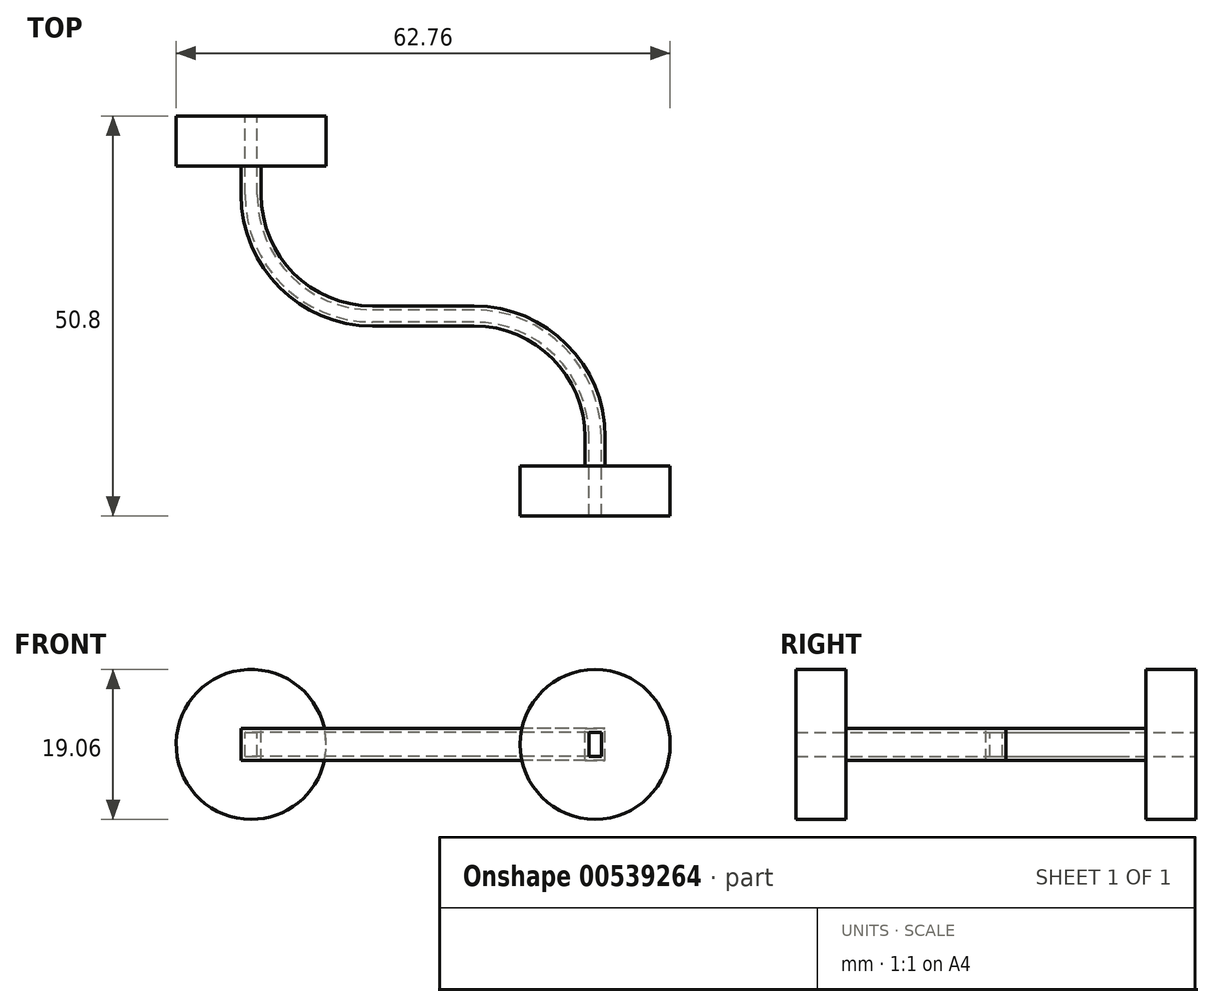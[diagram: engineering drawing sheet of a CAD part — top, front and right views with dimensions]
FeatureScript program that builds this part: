
annotation { "Feature Type Name" : "Feature", "Feature Type Description" : "" }
export const myFeature = defineFeature(function(context is Context, id is Id, definition is map)
    precondition{}
    {
        {
            var Q0;
            Q0=qCreatedBy(makeId("Top.planeOp"),FACE);
            var sketch = newSketch(context, id + "F0", { "sketchPlane" : qUnion([Q0])});
            skLineSegment(sketch, "E0", {"start": v(0, 0) * mm, "end": v(0, 10) * mm});
            skLineSegment(sketch, "E1", {"start": v(0, 0) * mm, "end": v(-21.85, 0) * mm});
            skLineSegment(sketch, "E2", {"start": v(-21.85, 0) * mm, "end": v(-21.85, 25.4) * mm});
            skLineSegment(sketch, "E3", {"start": v(-21.85, 25.4) * mm, "end": v(-15.4, 25.4) * mm});
            skLineSegment(sketch, "E4", {"start": v(-21.85, 25.4) * mm, "end": v(-28.3, 25.4) * mm});
            skLineSegment(sketch, "E5", {"start": v(-21.85, 25.4) * mm, "end": v(-21.85, 50.8) * mm});
            skLineSegment(sketch, "E6", {"start": v(-21.85, 50.8) * mm, "end": v(-43.7, 50.8) * mm});
            skLineSegment(sketch, "E7", {"start": v(-43.7, 50.8) * mm, "end": v(-43.7, 40.8) * mm});
            skArc(sketch, "E8", {"start": v(0, 10) * mm, "mid": v(-4.51, 20.89) * mm, "end": v(-15.4, 25.4) * mm});
            skArc(sketch, "E9", {"start": v(-43.7, 40.8) * mm, "mid": v(-39.19, 29.91) * mm, "end": v(-28.3, 25.4) * mm});
            skSolve(sketch);
        }
        {
            var Q0;
            Q0=qCreatedBy(makeId("Front.planeOp"),FACE);
            var sketch = newSketch(context, id + "F1", { "sketchPlane" : qUnion([Q0])});
            skLineSegment(sketch, "E10.bottom", {"start": v(-0.77, -1.55) * mm, "end": v(0.78, -1.55) * mm});
            skLineSegment(sketch, "E10.top", {"start": v(-0.78, 1.55) * mm, "end": v(0.77, 1.55) * mm});
            skLineSegment(sketch, "E10.left", {"start": v(-0.77, -1.55) * mm, "end": v(-0.78, 1.55) * mm});
            skLineSegment(sketch, "E10.right", {"start": v(0.78, -1.55) * mm, "end": v(0.77, 1.55) * mm});
            skPoint(sketch, "E10.middle", {"position": v(0, 0) * mm});
            skLineSegment(sketch, "E11.bottom", {"start": v(-1.27, -2.05) * mm, "end": v(1.28, -2.05) * mm});
            skLineSegment(sketch, "E11.top", {"start": v(-1.28, 2.05) * mm, "end": v(1.27, 2.05) * mm});
            skLineSegment(sketch, "E11.left", {"start": v(-1.27, -2.05) * mm, "end": v(-1.28, 2.05) * mm});
            skLineSegment(sketch, "E11.right", {"start": v(1.28, -2.05) * mm, "end": v(1.27, 2.05) * mm});
            skCircle(sketch, "E12", {"center": v(0, 0) * mm, "radius": 9.53 * mm});
            skSolve(sketch);
        }
        {
            var Q0;
            Q0=qCreatedBy(makeId("Front.planeOp"),FACE);
            cPlane(context, id + "F2", {"entities" : qUnion([Q0]), "cplaneType" : CPlaneType.OFFSET, "offset" : (25.4 * 2) * mm, "oppositeDirection" : true, "width" : 150 * mm, "height" : 150 * mm});
        }
        {
            var Q0;
            Q0=qCreatedBy(id+"F2.planeOp",FACE);
            var sketch = newSketch(context, id + "F3", { "sketchPlane" : qUnion([Q0])});
            skLineSegment(sketch, "E13.bottom", {"start": v(-42.93, -1.55) * mm, "end": v(-44.48, -1.55) * mm});
            skLineSegment(sketch, "E13.top", {"start": v(-42.93, 1.55) * mm, "end": v(-44.48, 1.55) * mm});
            skLineSegment(sketch, "E13.left", {"start": v(-42.93, -1.55) * mm, "end": v(-42.93, 1.55) * mm});
            skLineSegment(sketch, "E13.right", {"start": v(-44.48, -1.55) * mm, "end": v(-44.48, 1.55) * mm});
            skPoint(sketch, "E13.middle", {"position": v(-43.7, 0) * mm});
            skLineSegment(sketch, "E14.bottom", {"start": v(-42.43, -2.05) * mm, "end": v(-44.98, -2.05) * mm});
            skLineSegment(sketch, "E14.top", {"start": v(-42.43, 2.05) * mm, "end": v(-44.98, 2.05) * mm});
            skLineSegment(sketch, "E14.left", {"start": v(-42.43, -2.05) * mm, "end": v(-42.43, 2.05) * mm});
            skLineSegment(sketch, "E14.right", {"start": v(-44.98, -2.05) * mm, "end": v(-44.98, 2.05) * mm});
            skCircle(sketch, "E15", {"center": v(-43.7, 0) * mm, "radius": 9.53 * mm});
            skSolve(sketch);
        }
        {
            var Q0;
            Q0=makeQuery(id+"F1.imprint","IMPRINT",FACE,{"disambiguationData":[TD([[makeQuery(id+"F1.imprint","IMPRINT",EDGE,{"derivedFrom":sQuery(id+"F1.wireOp",EDGE,"E10.bottom")}),-1.0]])]});
            var Q1;
            Q1=sQuery(id+"F0.wireOp",EDGE,"E0");
            var Q2;
            Q2=sQuery(id+"F0.wireOp",EDGE,"E8");
            var Q3;
            Q3=sQuery(id+"F0.wireOp",EDGE,"E3");
            var Q4;
            Q4=sQuery(id+"F0.wireOp",EDGE,"E4");
            var Q5;
            Q5=sQuery(id+"F0.wireOp",EDGE,"E9");
            var Q6;
            Q6=sQuery(id+"F0.wireOp",EDGE,"E7");
            sweep(context, id + "F4", {"profiles" : qUnion([Q0]), "path" : qUnion([Q1, Q2, Q3, Q4, Q5, Q6])});
        }
        {
            var Q0;
            Q0 = qSketchRegion(id + "F1", true);
            extrude(context, id + "F5", {"entities" : qUnion([Q0]), "operationType" : NewBodyOperationType.ADD, "oppositeDirection" : true, "depth" : 6.35 * mm, "offsetDistance" : 25 * mm});
        }
        {
            var Q0;
            Q0 = qSketchRegion(id + "F3", true);
            extrude(context, id + "F6", {"entities" : qUnion([Q0]), "operationType" : NewBodyOperationType.ADD, "depth" : 6.35 * mm, "offsetDistance" : 25 * mm});
        }
    });
